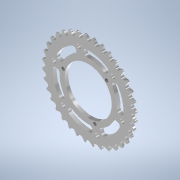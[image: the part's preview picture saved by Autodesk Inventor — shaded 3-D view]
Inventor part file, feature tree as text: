
AUTODESK INVENTOR PART (.ipt)
format: ipt  version: 2022.3 (Build 263350000, 350)  size: 1,098,752 bytes
history: native  units: in
note: dims shown in document units (in); Inventor stores cm internally (conversion verified against a paired STEP export)
features: sketch x4, extrude x2, hole x2, projected_geometry x2, fillet x1, pattern_circular x1, boolean_combine x1
ambient origin geometry x8: Origin, YZ Plane, XZ Plane, XY Plane, X Axis, Y Axis, Z Axis, Center Point
bodies: Solid1 (feature_tree)
feature tree (13):
  extrude  "Extrusion1"  TaperAngle=0.0deg  [1 undecoded]
  hole  "Hole1"  [1 undecoded]
  hole  "Hole2"  [1 undecoded]
  extrude  "Extrusion2"  Depth=0.13in TaperAngle=360.0deg
  fillet  "Fillet1"  Radius=4.0in
  pattern_circular  "Circular Pattern2"  [2 undecoded]
  sketch  "Sketch1"  dims[d0=2.25in d1=0.0in d2=0.0in]
  sketch  "Sketch2"  dims[d3=2.3622in d5=360.0deg d7=3.375in]
  sketch  "Sketch3"  dims[d8=0.201in d9=0.38in d10=0.385in d11=0.25in d12=0.563in d13=1.0in d14=0.8108in d15=0.24in]
  projected_geometry  "Projected Loop1"
  sketch  "Sketch5"  dims[d16=0.0in d17=1.1811in d19=360.0deg d21=0.156in d22=0.38in d23=0.385in d24=0.25in d25=0.563in d26=1.0in d27=0.8108in d28=4.0in d29=0.25in d30=3.5in d31=0.438in d32=0.25in d33=0.0in d34=0.0in d38=0.13in d39=2.3622in d40=2.4737in d18=0.15in d20=0.375in]
  projected_geometry  "Projected Loop2"
  boolean_combine  "Combine1"
note: 5 required parameter values undecoded (feature->parameter linkage not recoverable at this tier; creation-order binding heuristic only, values carry confidence <= 0.55)
